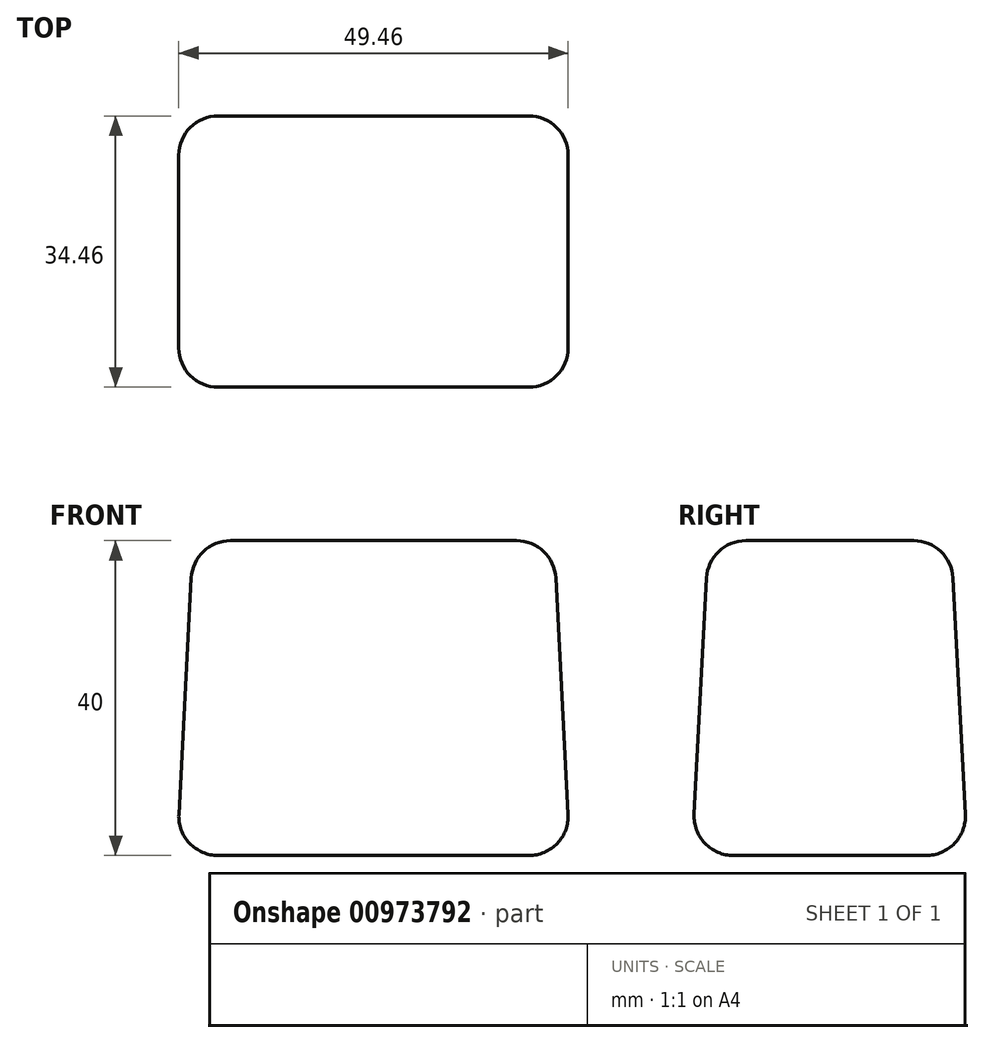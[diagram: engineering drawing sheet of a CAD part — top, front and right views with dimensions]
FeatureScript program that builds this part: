
annotation { "Feature Type Name" : "Feature", "Feature Type Description" : "" }
export const myFeature = defineFeature(function(context is Context, id is Id, definition is map)
    precondition{}
    {
        {
            var Q0;
            Q0=qCreatedBy(makeId("Top.planeOp"),FACE);
            var sketch = newSketch(context, id + "F0", { "sketchPlane" : qUnion([Q0])});
            skLineSegment(sketch, "E0.bottom", {"start": v(0, 0) * mm, "end": v(50, 0) * mm});
            skLineSegment(sketch, "E0.top", {"start": v(0, 35) * mm, "end": v(50, 35) * mm});
            skLineSegment(sketch, "E0.left", {"start": v(0, 0) * mm, "end": v(0, 35) * mm});
            skLineSegment(sketch, "E0.right", {"start": v(50, 0) * mm, "end": v(50, 35) * mm});
            skSolve(sketch);
        }
        {
            var Q0;
            Q0=makeQuery(id+"F0.imprint","IMPRINT",FACE,{"disambiguationData":[TD([[makeQuery(id+"F0.imprint","IMPRINT",EDGE,{"derivedFrom":sQuery(id+"F0.wireOp",EDGE,"E0.bottom")}),1.0]])]});
            extrude(context, id + "F1", {"entities" : qUnion([Q0]), "depth" : 40 * mm, "offsetDistance" : 25 * mm, "hasDraft" : true, "draftAngle" : 3 * degree, "draftPullDirection" : true});
        }
        {
            var Q0;
            Q0=makeQuery(id+"F1.opExtrude","SWEPT_EDGE",EDGE,{"disambiguationData":[OSD([sQuery(id+"F0.wireOp",EDGE,"E0.bottom"),sQuery(id+"F0.wireOp",EDGE,"E0.left")])]});
            var Q1;
            Q1=makeQuery(id+"F1.opExtrude","SWEPT_EDGE",EDGE,{"disambiguationData":[OSD([sQuery(id+"F0.wireOp",EDGE,"E0.bottom"),sQuery(id+"F0.wireOp",EDGE,"E0.right")])]});
            var Q2;
            Q2=makeQuery(id+"F1.opExtrude","SWEPT_EDGE",EDGE,{"disambiguationData":[OSD([sQuery(id+"F0.wireOp",EDGE,"E0.top"),sQuery(id+"F0.wireOp",EDGE,"E0.right")])]});
            var Q3;
            Q3=makeQuery(id+"F1.opExtrude","CAP_EDGE",EDGE,{"disambiguationData":[OSD([sQuery(id+"F0.wireOp",EDGE,"E0.bottom")])],"isStart":true});
            var Q4;
            Q4=makeQuery(id+"F1.opExtrude","CAP_EDGE",EDGE,{"disambiguationData":[OSD([sQuery(id+"F0.wireOp",EDGE,"E0.bottom")])],"isStart":false});
            var Q5;
            Q5=makeQuery(id+"F1.opExtrude","CAP_EDGE",EDGE,{"disambiguationData":[OSD([sQuery(id+"F0.wireOp",EDGE,"E0.top")])],"isStart":false});
            var Q6;
            Q6=makeQuery(id+"F1.opExtrude","CAP_EDGE",EDGE,{"disambiguationData":[OSD([sQuery(id+"F0.wireOp",EDGE,"E0.left")])],"isStart":false});
            var Q7;
            Q7=makeQuery(id+"F1.opExtrude","CAP_EDGE",EDGE,{"disambiguationData":[OSD([sQuery(id+"F0.wireOp",EDGE,"E0.right")])],"isStart":true});
            var Q8;
            Q8=makeQuery(id+"F1.opExtrude","CAP_EDGE",EDGE,{"disambiguationData":[OSD([sQuery(id+"F0.wireOp",EDGE,"E0.right")])],"isStart":false});
            var Q9;
            Q9=makeQuery(id+"F1.opExtrude","SWEPT_EDGE",EDGE,{"disambiguationData":[OSD([sQuery(id+"F0.wireOp",EDGE,"E0.top"),sQuery(id+"F0.wireOp",EDGE,"E0.left")])]});
            var Q10;
            Q10=makeQuery(id+"F1.opExtrude","CAP_EDGE",EDGE,{"disambiguationData":[OSD([sQuery(id+"F0.wireOp",EDGE,"E0.top")])],"isStart":true});
            var Q11;
            Q11=makeQuery(id+"F1.opExtrude","CAP_EDGE",EDGE,{"disambiguationData":[OSD([sQuery(id+"F0.wireOp",EDGE,"E0.left")])],"isStart":true});
            fillet(context, id + "F2", {"entities" : qUnion([Q0, Q1, Q2, Q3, Q4, Q5, Q6, Q7, Q8, Q9, Q10, Q11]), "radius" : 5 * mm, "tangentPropagation" : true, "allowEdgeOverflow" : false});
        }
    });
